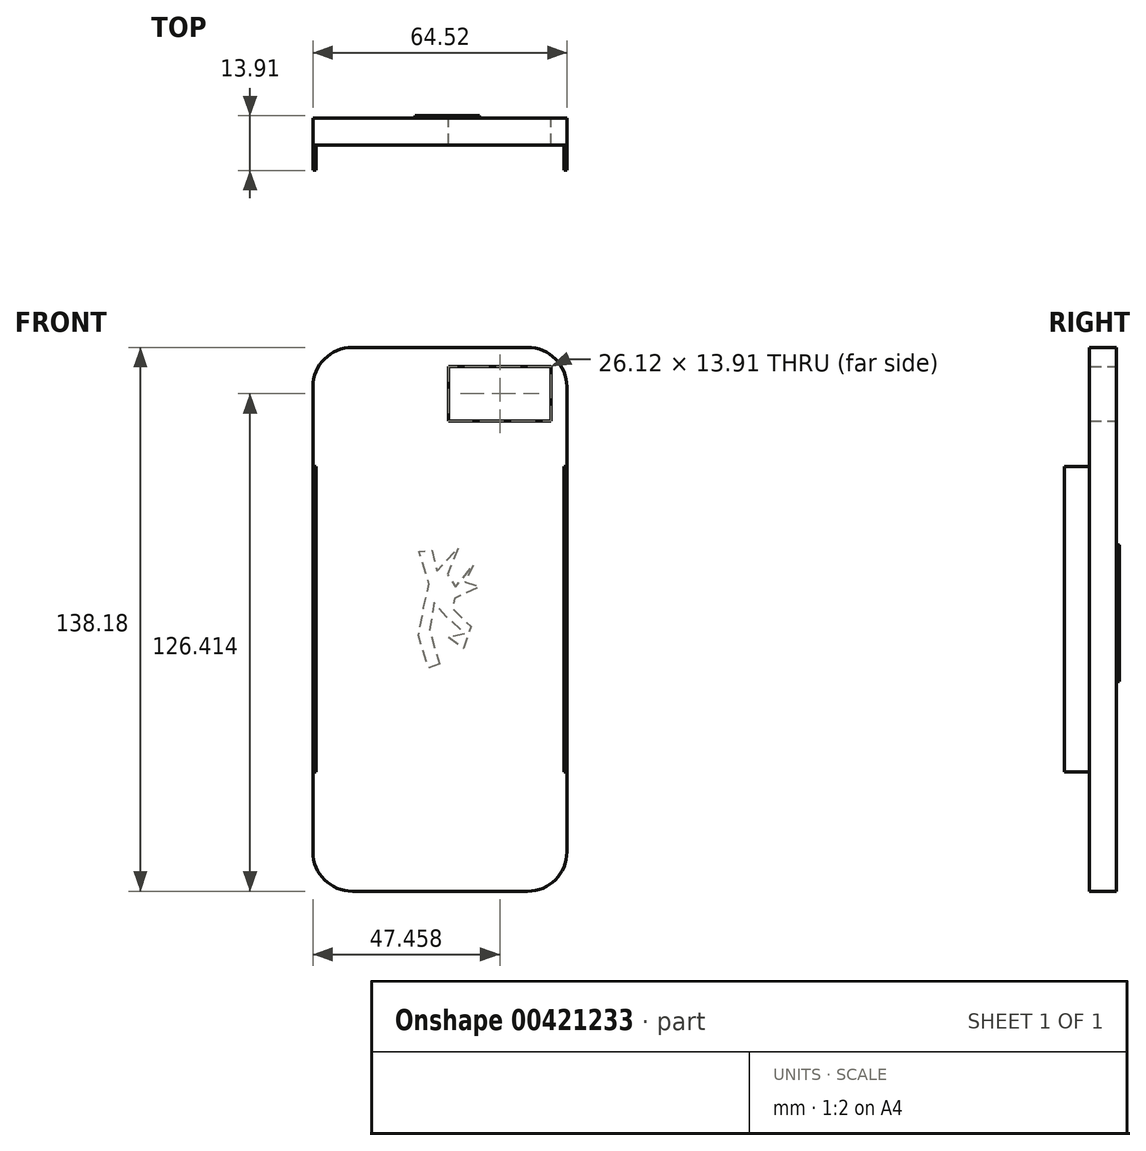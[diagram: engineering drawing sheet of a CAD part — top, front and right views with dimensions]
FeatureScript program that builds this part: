
annotation { "Feature Type Name" : "Feature", "Feature Type Description" : "" }
export const myFeature = defineFeature(function(context is Context, id is Id, definition is map)
    precondition{}
    {
        {
            var Q0;
            Q0=qCreatedBy(makeId("Front.planeOp"),FACE);
            var sketch = newSketch(context, id + "F0", { "sketchPlane" : qUnion([Q0])});
            skLineSegment(sketch, "E0", {"start": v(0, 59.1) * mm, "end": v(0, 0) * mm});
            skLineSegment(sketch, "E1", {"start": v(0, 0) * mm, "end": v(0, -59.1) * mm});
            skLineSegment(sketch, "E2", {"start": v(-9.98, 69.09) * mm, "end": v(-54.53, 69.09) * mm});
            skLineSegment(sketch, "E3", {"start": v(-64.52, 59.1) * mm, "end": v(-64.52, -59.1) * mm});
            skLineSegment(sketch, "E4", {"start": v(-54.53, -69.09) * mm, "end": v(-9.98, -69.09) * mm});
            skPoint(sketch, "E5.visualSharp", {"position": v(-64.52, 69.09) * mm});
            skArc(sketch, "E5.filletArc", {"start": v(-54.53, 69.09) * mm, "mid": v(-61.6, 66.16) * mm, "end": v(-64.52, 59.1) * mm});
            skPoint(sketch, "E6.visualSharp", {"position": v(0, 69.09) * mm});
            skArc(sketch, "E6.filletArc", {"start": v(0, 59.1) * mm, "mid": v(-2.92, 66.16) * mm, "end": v(-9.98, 69.09) * mm});
            skPoint(sketch, "E7.visualSharp", {"position": v(0, -69.09) * mm});
            skArc(sketch, "E7.filletArc", {"start": v(-9.98, -69.09) * mm, "mid": v(-2.92, -66.16) * mm, "end": v(0, -59.1) * mm});
            skPoint(sketch, "E8.visualSharp", {"position": v(-64.52, -69.09) * mm});
            skArc(sketch, "E8.filletArc", {"start": v(-64.52, -59.1) * mm, "mid": v(-61.6, -66.16) * mm, "end": v(-54.53, -69.09) * mm});
            skSolve(sketch);
        }
        {
            var Q0;
            Q0=makeQuery(id+"F0.imprint","IMPRINT",FACE,{"disambiguationData":[TD([[makeQuery(id+"F0.imprint","IMPRINT",EDGE,{"derivedFrom":sQuery(id+"F0.wireOp",EDGE,"E0")}),-1.0]])]});
            extrude(context, id + "F1", {"entities" : qUnion([Q0]), "depth" : 6.86 * mm});
        }
        {
            var Q0;
            Q0=qCreatedBy(makeId("Right.planeOp"),FACE);
            var sketch = newSketch(context, id + "F2", { "sketchPlane" : qUnion([Q0])});
            skLineSegment(sketch, "E9.0", {"start": v(-6.86, 59.1) * mm, "end": v(-6.86, -59.1) * mm});
            skLineSegment(sketch, "E10", {"start": v(-6.86, -38.79) * mm, "end": v(-13.2, -38.79) * mm});
            skLineSegment(sketch, "E11", {"start": v(-13.2, -38.79) * mm, "end": v(-13.2, 38.79) * mm});
            skLineSegment(sketch, "E12", {"start": v(-13.2, 38.79) * mm, "end": v(-6.86, 38.79) * mm});
            skLineSegment(sketch, "E13", {"start": v(-6.86, 38.79) * mm, "end": v(-13.2, 38.79) * mm});
            skLineSegment(sketch, "E14", {"start": v(-6.86, 38.79) * mm, "end": v(-6.86, -38.79) * mm});
            skSolve(sketch);
        }
        {
            var Q0;
            Q0=makeQuery(id+"F2.imprint","IMPRINT",FACE,{"disambiguationData":[TD([[makeQuery(id+"F2.imprint","IMPRINT",EDGE,{"derivedFrom":sQuery(id+"F2.wireOp",EDGE,"E10")}),-1.0]])]});
            extrude(context, id + "F3", {"entities" : qUnion([Q0]), "oppositeDirection" : true, "depth" : 0.76 * mm});
        }
        {
            var Q0;
            Q0=makeQuery(id+"F1.opExtrude","SWEPT_FACE",FACE,{"disambiguationData":[OSD([sQuery(id+"F0.wireOp",EDGE,"E3")])]});
            var sketch = newSketch(context, id + "F4", { "sketchPlane" : qUnion([Q0])});
            skLineSegment(sketch, "E15.0.0", {"start": v(6.86, 38.79) * mm, "end": v(6.86, -38.79) * mm});
            skLineSegment(sketch, "E15.0.1", {"start": v(6.86, -38.79) * mm, "end": v(13.2, -38.79) * mm});
            skLineSegment(sketch, "E15.0.2", {"start": v(13.2, -38.79) * mm, "end": v(13.2, 38.79) * mm});
            skLineSegment(sketch, "E15.0.3", {"start": v(13.2, 38.79) * mm, "end": v(6.86, 38.79) * mm});
            skSolve(sketch);
        }
        {
            var Q0;
            Q0 = qSketchRegion(id + "F4", true);
            extrude(context, id + "F5", {"entities" : qUnion([Q0]), "operationType" : NewBodyOperationType.ADD, "oppositeDirection" : true, "depth" : 0.76 * mm});
        }
        {
            var Q0;
            Q0=makeQuery(id+"F1.opExtrude","CAP_FACE",FACE,{"disambiguationData":[OSD([sQuery(id+"F0.wireOp",EDGE,"E0"),sQuery(id+"F0.wireOp",EDGE,"E1"),sQuery(id+"F0.wireOp",EDGE,"E2"),sQuery(id+"F0.wireOp",EDGE,"E3"),sQuery(id+"F0.wireOp",EDGE,"E4"),sQuery(id+"F0.wireOp",EDGE,"E5.filletArc"),sQuery(id+"F0.wireOp",EDGE,"E6.filletArc"),sQuery(id+"F0.wireOp",EDGE,"E7.filletArc"),sQuery(id+"F0.wireOp",EDGE,"E8.filletArc")])],"isStart":true});
            var sketch = newSketch(context, id + "F6", { "sketchPlane" : qUnion([Q0])});
            skLineSegment(sketch, "E16.bottom", {"start": v(4, 64.28) * mm, "end": v(30.12, 64.28) * mm});
            skLineSegment(sketch, "E16.top", {"start": v(4, 50.37) * mm, "end": v(30.12, 50.37) * mm});
            skLineSegment(sketch, "E16.left", {"start": v(4, 64.28) * mm, "end": v(4, 50.37) * mm});
            skLineSegment(sketch, "E16.right", {"start": v(30.12, 64.28) * mm, "end": v(30.12, 50.37) * mm});
            skSolve(sketch);
        }
        {
            var Q0;
            Q0=makeQuery(id+"F6.imprint","IMPRINT",FACE,{"disambiguationData":[TD([[makeQuery(id+"F6.imprint","IMPRINT",EDGE,{"derivedFrom":sQuery(id+"F6.wireOp",EDGE,"E16.bottom")}),-1.0]])]});
            extrude(context, id + "F7", {"entities" : qUnion([Q0]), "operationType" : NewBodyOperationType.REMOVE, "oppositeDirection" : true, "depth" : 25 * mm});
        }
        {
            var Q0;
            Q0=makeQuery(id+"F1.opExtrude","CAP_FACE",FACE,{"disambiguationData":[OSD([sQuery(id+"F0.wireOp",EDGE,"E0"),sQuery(id+"F0.wireOp",EDGE,"E1"),sQuery(id+"F0.wireOp",EDGE,"E2"),sQuery(id+"F0.wireOp",EDGE,"E3"),sQuery(id+"F0.wireOp",EDGE,"E4"),sQuery(id+"F0.wireOp",EDGE,"E5.filletArc"),sQuery(id+"F0.wireOp",EDGE,"E6.filletArc"),sQuery(id+"F0.wireOp",EDGE,"E7.filletArc"),sQuery(id+"F0.wireOp",EDGE,"E8.filletArc")])],"isStart":true});
            var sketch = newSketch(context, id + "F8", { "sketchPlane" : qUnion([Q0])});
            skFitSpline(sketch, "E17", {"points": [v(32.38, -11.34) * mm, v(32.4, -15.64) * mm, v(32.96, -15.66) * mm, v(33.53, -15.39) * mm, v(34.63, -13.68) * mm, v(35.22, -12.3) * mm, v(36.42, -11.15) * mm, v(37.18, -9.66) * mm, v(38.02, -7.1) * mm, v(37.9, -5.2) * mm, v(37.23, -2.22) * mm, v(35.92, -0.46) * mm, v(34.94, 0.9) * mm, v(35.68, 1.44) * mm, v(36.27, 2.55) * mm, v(36.42, 4.33) * mm, v(35.67, 6.25) * mm, v(35.41, 7.04) * mm, v(33.58, 7.8) * mm, v(34.43, 8.57) * mm, v(36.43, 10.37) * mm, v(37.87, 12.18) * mm, v(38.54, 14.57) * mm, v(38.03, 16.65) * mm, v(36.88, 18.02) * mm, v(35.55, 18.72) * mm, v(33.81, 18.81) * mm, v(32.68, 18.4) * mm, v(33.46, 18.1) * mm, v(34.4, 17.4) * mm, v(35.33, 16.54) * mm, v(35.86, 14.91) * mm, v(35.32, 13.2) * mm, v(34.4, 12.48) * mm, v(33.28, 12.23) * mm, v(31.9, 12.82) * mm, v(30.3, 14.42) * mm, v(28.72, 16.3) * mm, v(28.29, 17.32) * mm, v(27.64, 18.17) * mm, v(27.39, 17.06) * mm, v(27.53, 15.77) * mm, v(27.89, 14.14) * mm, v(29.03, 12.6) * mm, v(30.18, 11.57) * mm, v(31.1, 10.32) * mm, v(31.42, 8.97) * mm, v(30.9, 8.1) * mm, v(30.04, 7.55) * mm, v(29.09, 7.57) * mm, v(28.32, 8.2) * mm, v(27.8, 9.95) * mm, v(27.5, 11.41) * mm, v(26.62, 12.66) * mm, v(25.24, 13.53) * mm, v(23.73, 13.96) * mm, v(22.16, 13.71) * mm, v(23.05, 13.52) * mm, v(24.16, 12.77) * mm, v(25.09, 11.8) * mm, v(25.78, 10.16) * mm, v(25.74, 8.38) * mm, v(24.95, 7.78) * mm, v(23.93, 7.58) * mm, v(23.28, 8.26) * mm, v(22.8, 9.34) * mm, v(22.33, 8.73) * mm, v(22.36, 7.56) * mm, v(23.07, 6.42) * mm, v(24.96, 5.66) * mm, v(27.14, 5.66) * mm, v(28.26, 5.58) * mm, v(28.75, 4.95) * mm, v(28.46, 4.3) * mm, v(27.67, 4.25) * mm, v(27.17, 4.32) * mm, v(27.16, 3.87) * mm, v(27.71, 3.47) * mm, v(28.04, 3.18) * mm, v(28.71, 3.05) * mm, v(28.97, 2.04) * mm, v(28.02, 2) * mm, v(27.5, 1.74) * mm, v(25.46, 0) * mm, v(25.44, -0.78) * mm, v(24.86, -1.44) * mm, v(23.43, -2.97) * mm, v(22.52, -5.97) * mm, v(24.35, -7.08) * mm, v(25.53, -7) * mm, v(26.14, -7.4) * mm, v(26.81, -7.19) * mm, v(27.44, -6.7) * mm, v(30.3, -6.82) * mm, v(30.93, -6.05) * mm, v(30.8, -4.37) * mm, v(30.12, -4.47) * mm, v(29.06, -4.44) * mm, v(27.55, -4.35) * mm, v(26.23, -5.44) * mm, v(24.95, -5.08) * mm, v(25.6, -3.92) * mm, v(27.08, -2.39) * mm, v(27.76, -2.01) * mm, v(27.73, -1.12) * mm, v(28.3, -0.46) * mm, v(29.67, 0.69) * mm, v(30.62, 0.66) * mm, v(31.09, 1.32) * mm, v(31.1, 2.16) * mm, v(30.95, 2.9) * mm, v(31.59, 3.94) * mm, v(33.3, 5.24) * mm, v(33.84, 4.17) * mm, v(33.58, 2.72) * mm, v(32.61, 1.9) * mm, v(32.4, 0) * mm, v(33.94, -1.37) * mm, v(35.18, -3.58) * mm, v(35.46, -6.49) * mm, v(34.5, -9.32) * mm, v(32.9, -11.01) * mm, v(32.38, -11.34) * mm]});
            skSolve(sketch);
        }
        {
            var Q0;
            Q0=makeQuery(id+"F8.imprint","IMPRINT",FACE,{"disambiguationData":[TD([[makeQuery(id+"F8.imprint","IMPRINT",EDGE,{"derivedFrom":sQuery(id+"F8.wireOp",EDGE,"E17")}),1.0]])]});
            extrude(context, id + "F9", {"entities" : qUnion([Q0]), "depth" : .7 * mm});
        }
    });
